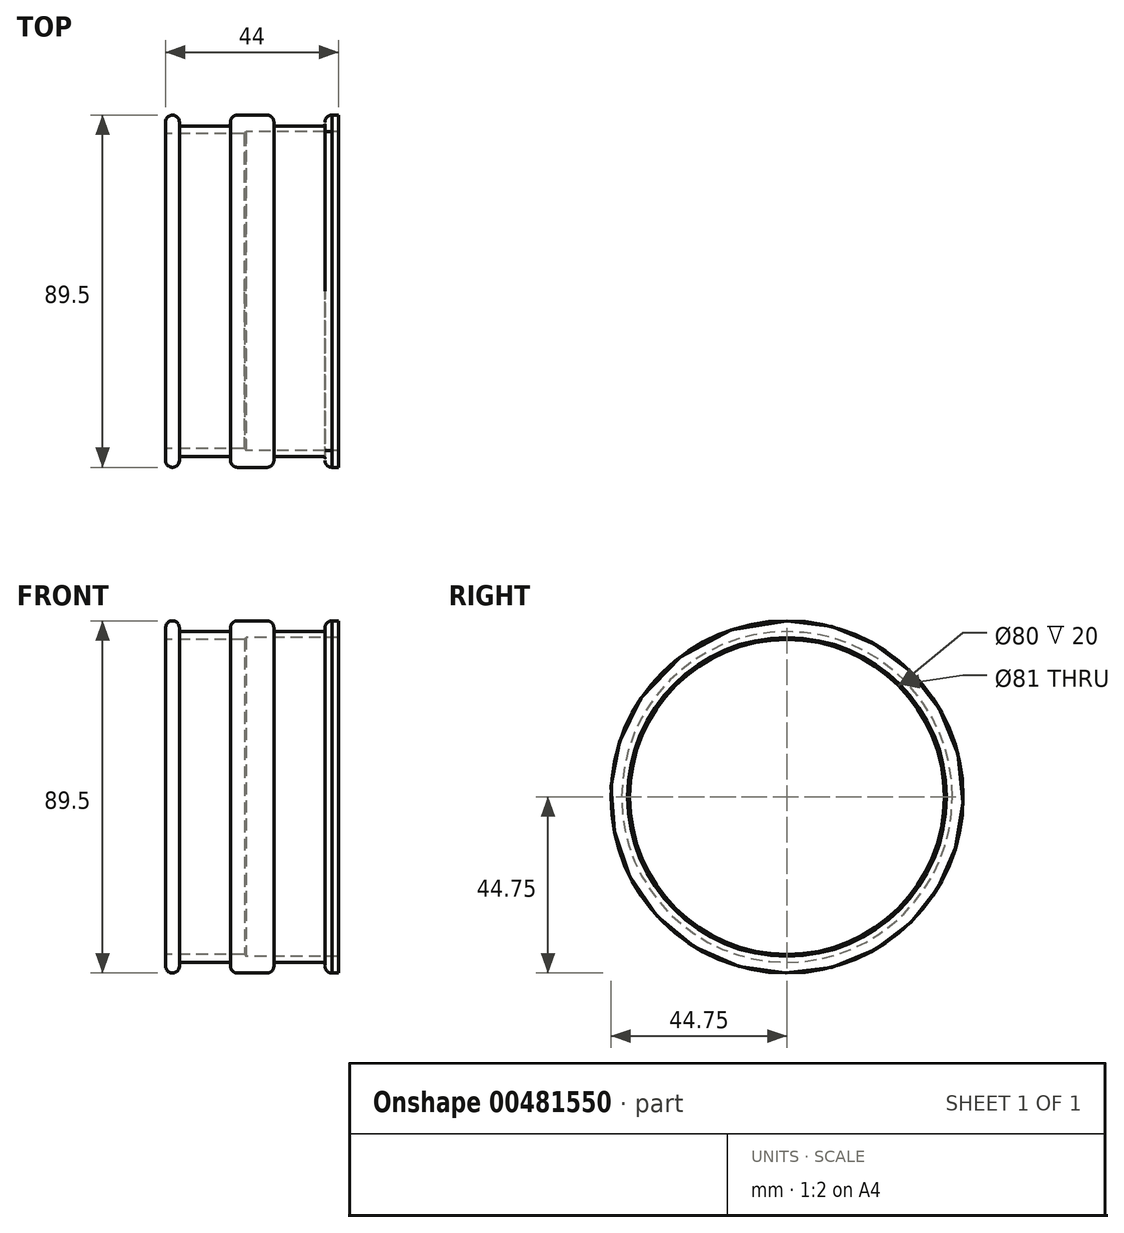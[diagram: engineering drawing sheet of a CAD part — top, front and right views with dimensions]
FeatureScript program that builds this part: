
annotation { "Feature Type Name" : "Feature", "Feature Type Description" : "" }
export const myFeature = defineFeature(function(context is Context, id is Id, definition is map)
    precondition{}
    {
        {
            var Q0;
            Q0=qCreatedBy(makeId("Front.planeOp"),FACE);
            var sketch = newSketch(context, id + "F0", { "sketchPlane" : qUnion([Q0])});
            skLineSegment(sketch, "E0", {"start": v(-51.49, 40) * mm, "end": v(-31.49, 40) * mm});
            skLineSegment(sketch, "E1", {"start": v(-51.49, 40) * mm, "end": v(-51.49, 41) * mm});
            skLineSegment(sketch, "E2", {"start": v(-71.44, 0) * mm, "end": v(11.8, 0) * mm, "construction": true});
            skLineSegment(sketch, "E3", {"start": v(-32.49, 40) * mm, "end": v(-32.49, 38.1) * mm, "construction": true});
            skLineSegment(sketch, "E4", {"start": v(-32.49, 38.1) * mm, "end": v(-57.12, 38.1) * mm, "construction": true});
            skLineSegment(sketch, "E5", {"start": v(-51.49, 40) * mm, "end": v(-57.12, 40) * mm, "construction": true});
            skLineSegment(sketch, "E6", {"start": v(-28.6, 40) * mm, "end": v(-28.6, 37.92) * mm, "construction": true});
            skLineSegment(sketch, "E7", {"start": v(-28.6, 37.92) * mm, "end": v(-6.82, 37.92) * mm, "construction": true});
            skLineSegment(sketch, "E8", {"start": v(-34.99, 42.31) * mm, "end": v(-34.99, 39.35) * mm, "construction": true});
            skLineSegment(sketch, "E9", {"start": v(-30.99, 40.5) * mm, "end": v(-7.49, 40.5) * mm});
            skPoint(sketch, "E9.endSnap0", {"position": v(-10.99, 40.5) * mm});
            skPoint(sketch, "E10", {"position": v(-49.74, 43) * mm});
            skPoint(sketch, "E11", {"position": v(-47.99, 43) * mm});
            skArc(sketch, "E12", {"start": v(-33.24, 44.75) * mm, "mid": v(-34.47, 44.24) * mm, "end": v(-34.99, 43) * mm});
            skArc(sketch, "E13", {"start": v(-23.99, 43) * mm, "mid": v(-24.5, 44.24) * mm, "end": v(-25.74, 44.75) * mm});
            skArc(sketch, "E14", {"start": v(-9.18, 44.75) * mm, "mid": v(-10.45, 44.26) * mm, "end": v(-10.99, 43) * mm});
            skLineSegment(sketch, "E15", {"start": v(-9.18, 44.75) * mm, "end": v(-7.5, 44.75) * mm});
            skLineSegment(sketch, "E16", {"start": v(-10.99, 43.08) * mm, "end": v(-10.99, 42.5) * mm});
            skLineSegment(sketch, "E17.trimOffspring", {"start": v(-7.5, 43) * mm, "end": v(-7.49, 43) * mm, "construction": true});
            skLineSegment(sketch, "E18.trimOffspring", {"start": v(-23.99, 37.92) * mm, "end": v(-23.99, 37.53) * mm, "construction": true});
            skLineSegment(sketch, "E19", {"start": v(-23.99, 43) * mm, "end": v(-23.99, 42.5) * mm});
            skLineSegment(sketch, "E20", {"start": v(-23.49, 42) * mm, "end": v(-11.49, 42) * mm});
            skLineSegment(sketch, "E21.trimOffspring", {"start": v(-23.49, 42) * mm, "end": v(-11.49, 42) * mm, "construction": true});
            skPoint(sketch, "E22.start.orphan", {"position": v(-24.5, 42) * mm});
            skPoint(sketch, "E23.visualSharp", {"position": v(-23.99, 42) * mm});
            skArc(sketch, "E23.filletArc", {"start": v(-23.99, 42.5) * mm, "mid": v(-23.84, 42.15) * mm, "end": v(-23.49, 42) * mm});
            skPoint(sketch, "E24.visualSharp", {"position": v(-10.99, 42) * mm});
            skArc(sketch, "E24.filletArc", {"start": v(-11.49, 42) * mm, "mid": v(-11.13, 42.15) * mm, "end": v(-10.99, 42.5) * mm});
            skLineSegment(sketch, "E25", {"start": v(-33.24, 44.75) * mm, "end": v(-25.74, 44.75) * mm});
            skLineSegment(sketch, "E26", {"start": v(-47.49, 42) * mm, "end": v(-35.49, 42) * mm});
            skPoint(sketch, "E27.orphan", {"position": v(-33.34, 42) * mm});
            skLineSegment(sketch, "E28", {"start": v(-47.99, 43) * mm, "end": v(-47.99, 42.5) * mm});
            skLineSegment(sketch, "E29", {"start": v(-34.99, 43) * mm, "end": v(-34.99, 42.5) * mm});
            skPoint(sketch, "E30.visualSharp", {"position": v(-47.98, 42) * mm});
            skArc(sketch, "E30.filletArc", {"start": v(-47.99, 42.5) * mm, "mid": v(-47.84, 42.15) * mm, "end": v(-47.49, 42) * mm});
            skPoint(sketch, "E31.visualSharp", {"position": v(-34.99, 42) * mm});
            skArc(sketch, "E31.filletArc", {"start": v(-35.49, 42) * mm, "mid": v(-35.13, 42.15) * mm, "end": v(-34.99, 42.5) * mm});
            skPoint(sketch, "E32", {"position": v(-51.49, 43) * mm});
            skArc(sketch, "E33", {"start": v(-47.99, 43) * mm, "mid": v(-49.74, 44.75) * mm, "end": v(-51.49, 43) * mm});
            skLineSegment(sketch, "E34", {"start": v(-51.49, 43) * mm, "end": v(-51.49, 41) * mm});
            skPoint(sketch, "E35.trimOffspring.end.orphan", {"position": v(-47.99, 39.35) * mm});
            skPoint(sketch, "E36.end.orphan", {"position": v(-47.1, 43) * mm});
            skPoint(sketch, "E37.start.orphan", {"position": v(-47.99, 42.13) * mm});
            skLineSegment(sketch, "E38", {"start": v(-7.5, 44.75) * mm, "end": v(-7.49, 40.5) * mm});
            skLineSegment(sketch, "E39", {"start": v(-31.49, 40) * mm, "end": v(-30.99, 40.5) * mm});
            skSolve(sketch);
        }
        {
            var Q0;
            Q0=makeQuery(id+"F0.imprint","IMPRINT",FACE,{"disambiguationData":[TD([[makeQuery(id+"F0.imprint","IMPRINT",EDGE,{"derivedFrom":sQuery(id+"F0.wireOp",EDGE,"E0")}),1.0]])]});
            var Q1;
            Q1=sQuery(id+"F0.wireOp",EDGE,"E2");
            revolve(context, id + "F1", {"entities" : qUnion([Q0]), "axis" : qUnion([Q1]), "revolveType" : RevolveType.FULL});
        }
    });
